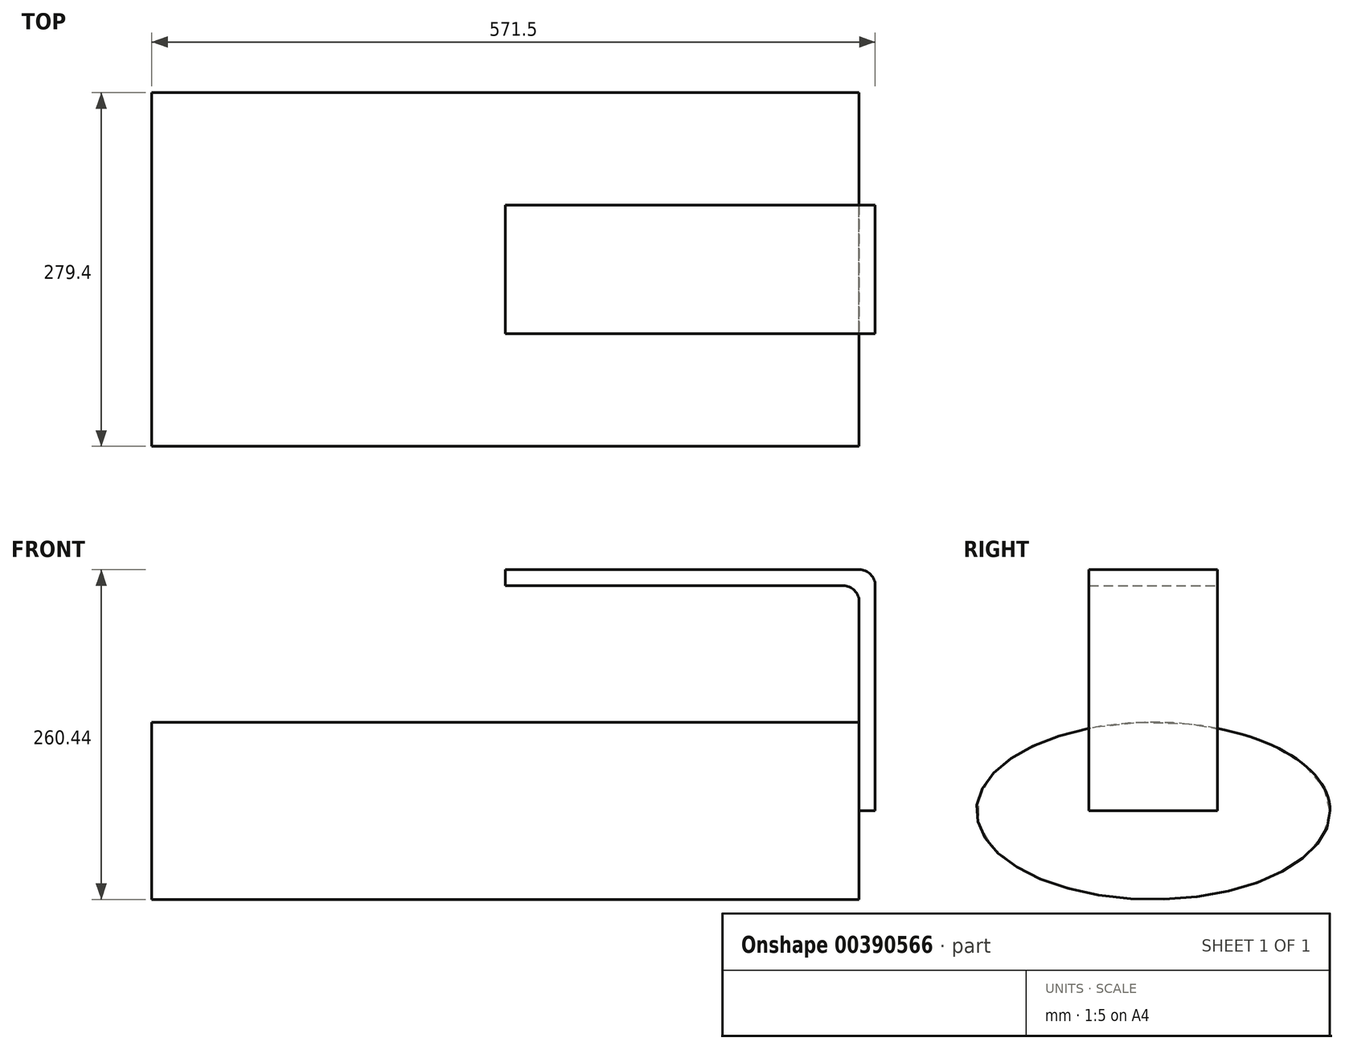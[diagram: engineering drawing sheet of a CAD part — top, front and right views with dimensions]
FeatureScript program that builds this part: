
annotation { "Feature Type Name" : "Feature", "Feature Type Description" : "" }
export const myFeature = defineFeature(function(context is Context, id is Id, definition is map)
    precondition{}
    {
        {
            var Q0;
            Q0=qCreatedBy(makeId("Right.planeOp"),FACE);
            var sketch = newSketch(context, id + "F0", { "sketchPlane" : qUnion([Q0])});
            skEllipse(sketch, "E0", {"center": v(0, 0) * mm, "majorRadius": 139.7 * mm, "minorRadius": 69.94 * mm, "majorAxis": v(1, 0)});
            skLineSegment(sketch, "E1", {"start": v(-139.7, 0) * mm, "end": v(139.7, 0) * mm, "construction": true});
            skSolve(sketch);
        }
        {
            var Q0;
            Q0 = qSketchRegion(id + "F0", true);
            extrude(context, id + "F1", {"entities" : qUnion([Q0]), "depth" : 279.4 * mm, "hasSecondDirection" : true, "secondDirectionOppositeDirection" : true, "secondDirectionDepth" : 279.4 * mm});
        }
        {
            var Q0;
            Q0=qCreatedBy(makeId("Front.planeOp"),FACE);
            var sketch = newSketch(context, id + "F2", { "sketchPlane" : qUnion([Q0])});
            skLineSegment(sketch, "E2", {"start": v(0, 0) * mm, "end": v(0, 190.5) * mm});
            skLineSegment(sketch, "E3", {"start": v(0, 190.5) * mm, "end": v(279.4, 190.5) * mm});
            skLineSegment(sketch, "E4", {"start": v(292.1, 177.8) * mm, "end": v(292.1, 0) * mm});
            skPoint(sketch, "E5.visualSharp", {"position": v(292.1, 190.5) * mm});
            skArc(sketch, "E5.filletArc", {"start": v(292.1, 177.8) * mm, "mid": v(288.38, 186.78) * mm, "end": v(279.4, 190.5) * mm});
            skLineSegment(sketch, "E6.0", {"start": v(279.4, 165.1) * mm, "end": v(279.4, 0) * mm});
            skLineSegment(sketch, "E6.1", {"start": v(0, 177.8) * mm, "end": v(266.7, 177.8) * mm});
            skArc(sketch, "E7.MirrorCS", {"start": v(-292.1, 177.8) * mm, "mid": v(-288.38, 186.78) * mm, "end": v(-279.4, 190.5) * mm});
            skLineSegment(sketch, "E8.MirrorCS", {"start": v(0, 190.5) * mm, "end": v(-279.4, 190.5) * mm});
            skLineSegment(sketch, "E9.MirrorCS", {"start": v(0, 177.8) * mm, "end": v(-266.7, 177.8) * mm});
            skLineSegment(sketch, "E10.MirrorCS", {"start": v(-292.1, 177.8) * mm, "end": v(-292.1, 0) * mm});
            skLineSegment(sketch, "E11.MirrorCS", {"start": v(-279.4, 165.1) * mm, "end": v(-279.4, 0) * mm});
            skPoint(sketch, "E12.MirrorP", {"position": v(-292.1, 190.5) * mm});
            skArc(sketch, "E13.filletArc", {"start": v(279.4, 165.1) * mm, "mid": v(275.68, 174.08) * mm, "end": v(266.7, 177.8) * mm});
            skArc(sketch, "E14.filletArc", {"start": v(-266.7, 177.8) * mm, "mid": v(-275.68, 174.08) * mm, "end": v(-279.4, 165.1) * mm});
            skLineSegment(sketch, "E15", {"start": v(-292.1, 0) * mm, "end": v(-279.4, 0) * mm});
            skLineSegment(sketch, "E16", {"start": v(279.4, 0) * mm, "end": v(292.1, 0) * mm});
            skSolve(sketch);
        }
        {
            var Q0;
            Q0=makeQuery(id+"F2.imprint","IMPRINT",FACE,{"disambiguationData":[TD([[makeQuery(id+"F2.imprint","IMPRINT",EDGE,{"derivedFrom":sQuery(id+"F2.wireOp",EDGE,"E7.MirrorCS")}),-1.0]])]});
            var Q1;
            {var subQ0=sQuery(id+"F2.wireOp",EDGE,"E3");Q1=makeQuery(id+"F2.imprint","IMPRINT",FACE,{"disambiguationData":[TD([[makeQuery(id+"F2.imprint","IMPRINT",EDGE,{"derivedFrom":subQ0}),-1.0]])]});}
            extrude(context, id + "F3", {"entities" : qUnion([Q0, Q1]), "depth" : 50.8 * mm, "hasSecondDirection" : true, "secondDirectionOppositeDirection" : true, "secondDirectionDepth" : 50.8 * mm});
        }
    });
